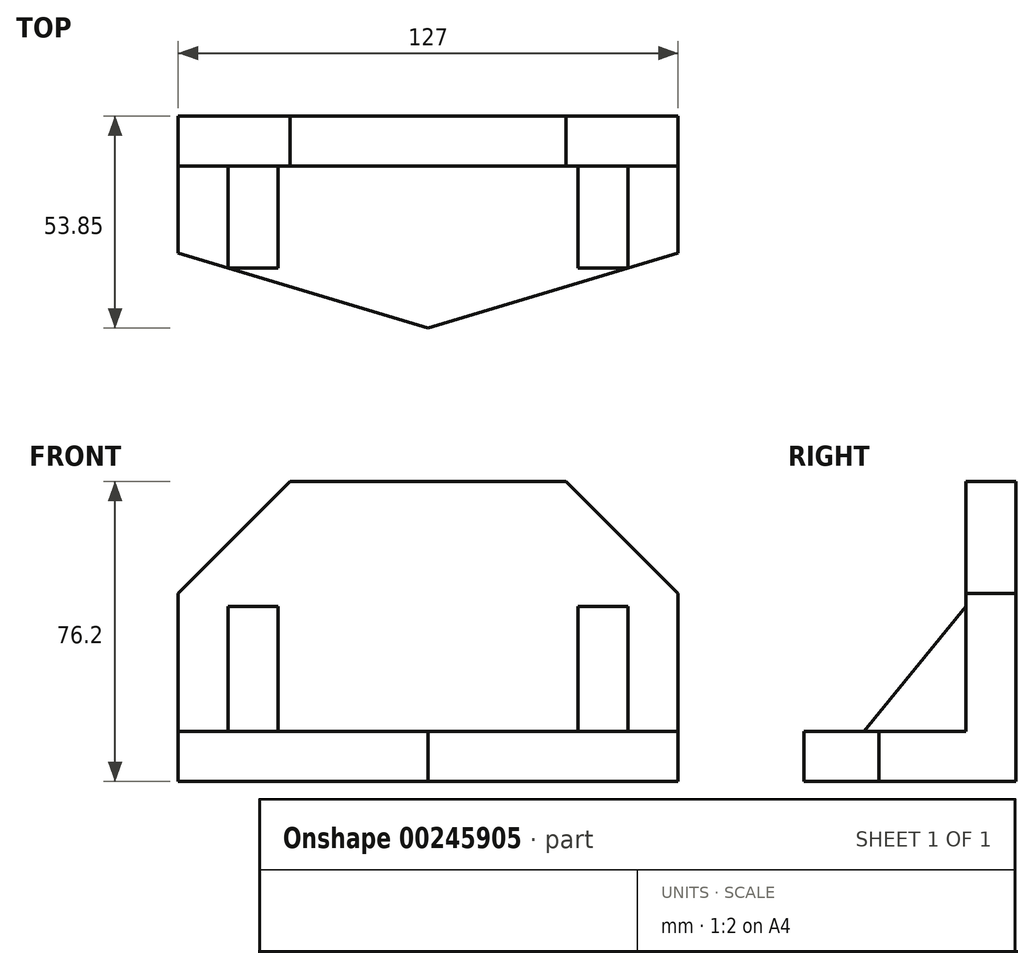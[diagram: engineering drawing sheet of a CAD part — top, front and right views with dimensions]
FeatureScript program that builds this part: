
annotation { "Feature Type Name" : "Feature", "Feature Type Description" : "" }
export const myFeature = defineFeature(function(context is Context, id is Id, definition is map)
    precondition{}
    {
        {
            var Q0;
            Q0=qCreatedBy(makeId("Front.planeOp"),FACE);
            var sketch = newSketch(context, id + "F0", { "sketchPlane" : qUnion([Q0])});
            skLineSegment(sketch, "E0", {"start": v(-81, -38.68) * mm, "end": v(46, -38.68) * mm});
            skLineSegment(sketch, "E1", {"start": v(46, -38.68) * mm, "end": v(46, 37.52) * mm});
            skLineSegment(sketch, "E2", {"start": v(46, 37.52) * mm, "end": v(-81, 37.52) * mm});
            skLineSegment(sketch, "E3", {"start": v(-81, 37.52) * mm, "end": v(-81, -38.68) * mm});
            skSolve(sketch);
        }
        {
            var Q0;
            Q0 = qSketchRegion(id + "F0", true);
            extrude(context, id + "F1", {"entities" : qUnion([Q0]), "depth" : 53.85 * mm});
        }
        {
            var Q0;
            Q0=makeQuery(id+"F1.opExtrude","SWEPT_FACE",FACE,{"disambiguationData":[OSD([sQuery(id+"F0.wireOp",EDGE,"E1")])]});
            var sketch = newSketch(context, id + "F2", { "sketchPlane" : qUnion([Q0])});
            skLineSegment(sketch, "E4", {"start": v(-53.85, 37.52) * mm, "end": v(-12.7, 37.52) * mm});
            skLineSegment(sketch, "E5", {"start": v(-12.7, 37.52) * mm, "end": v(-12.7, -25.98) * mm});
            skLineSegment(sketch, "E6", {"start": v(-12.7, -25.98) * mm, "end": v(-53.85, -25.98) * mm});
            skLineSegment(sketch, "E7", {"start": v(-53.85, -25.98) * mm, "end": v(-53.85, 37.52) * mm});
            skSolve(sketch);
        }
        {
            var Q0;
            Q0 = qSketchRegion(id + "F2", true);
            extrude(context, id + "F3", {"entities" : qUnion([Q0]), "operationType" : NewBodyOperationType.REMOVE, "oppositeDirection" : true, "depth" : 127 * mm});
        }
        {
            var Q0;
            Q0=makeQuery(id+"F3.boolean.opBoolean","COPY",FACE,{"derivedFrom":makeQuery(id+"F3.opExtrude","SWEPT_FACE",FACE,{"disambiguationData":[OSD([sQuery(id+"F2.wireOp",EDGE,"E5")])]})});
            var sketch = newSketch(context, id + "F4", { "sketchPlane" : qUnion([Q0])});
            skLineSegment(sketch, "E8", {"start": v(46, 37.52) * mm, "end": v(17.55, 37.52) * mm});
            skLineSegment(sketch, "E9", {"start": v(46, 37.52) * mm, "end": v(46, 9.07) * mm});
            skLineSegment(sketch, "E10", {"start": v(17.55, 37.52) * mm, "end": v(46, 9.07) * mm});
            skLineSegment(sketch, "E11", {"start": v(-81, 37.52) * mm, "end": v(-52.56, 37.52) * mm});
            skLineSegment(sketch, "E12", {"start": v(-81, 37.52) * mm, "end": v(-81, 9.07) * mm});
            skLineSegment(sketch, "E13", {"start": v(-52.56, 37.52) * mm, "end": v(-81, 9.07) * mm});
            skSolve(sketch);
        }
        {
            var Q0;
            Q0 = qSketchRegion(id + "F4", true);
            extrude(context, id + "F5", {"entities" : qUnion([Q0]), "operationType" : NewBodyOperationType.REMOVE, "oppositeDirection" : true, "depth" : 12.7 * mm});
        }
        {
            var Q0;
            Q0=makeQuery(id+"F3.boolean.opBoolean","COPY",FACE,{"derivedFrom":makeQuery(id+"F3.opExtrude","SWEPT_FACE",FACE,{"disambiguationData":[OSD([sQuery(id+"F2.wireOp",EDGE,"E6")])]})});
            var sketch = newSketch(context, id + "F6", { "sketchPlane" : qUnion([Q0])});
            skLineSegment(sketch, "E14", {"start": v(-17.5, -53.85) * mm, "end": v(46, -53.85) * mm});
            skLineSegment(sketch, "E15", {"start": v(-17.5, -53.85) * mm, "end": v(-81, -53.85) * mm});
            skLineSegment(sketch, "E16", {"start": v(46, -53.85) * mm, "end": v(46, -34.8) * mm});
            skLineSegment(sketch, "E17", {"start": v(-17.5, -53.85) * mm, "end": v(46, -34.8) * mm});
            skLineSegment(sketch, "E18", {"start": v(-81, -53.85) * mm, "end": v(-81, -34.8) * mm});
            skLineSegment(sketch, "E19", {"start": v(-81, -34.8) * mm, "end": v(-17.5, -53.85) * mm});
            skSolve(sketch);
        }
        {
            var Q0;
            Q0 = qSketchRegion(id + "F6", true);
            extrude(context, id + "F7", {"entities" : qUnion([Q0]), "operationType" : NewBodyOperationType.REMOVE, "oppositeDirection" : true, "depth" : 12.7 * mm});
        }
        {
            var Q0;
            Q0=makeQuery(id+"F3.boolean.opBoolean","COPY",FACE,{"derivedFrom":makeQuery(id+"F3.opExtrude","SWEPT_FACE",FACE,{"disambiguationData":[OSD([sQuery(id+"F2.wireOp",EDGE,"E6")])]})});
            var sketch = newSketch(context, id + "F8", { "sketchPlane" : qUnion([Q0])});
            skLineSegment(sketch, "E20", {"start": v(46, -12.7) * mm, "end": v(33.3, -12.7) * mm});
            skLineSegment(sketch, "E21", {"start": v(33.3, -12.7) * mm, "end": v(33.3, -38.6) * mm});
            skLineSegment(sketch, "E22", {"start": v(33.3, -38.6) * mm, "end": v(20.6, -38.6) * mm});
            skLineSegment(sketch, "E23", {"start": v(20.6, -38.6) * mm, "end": v(20.6, -12.7) * mm});
            skLineSegment(sketch, "E24", {"start": v(20.6, -12.7) * mm, "end": v(33.3, -12.7) * mm});
            skLineSegment(sketch, "E25", {"start": v(-81, -12.7) * mm, "end": v(-68.3, -12.7) * mm});
            skLineSegment(sketch, "E26", {"start": v(-68.3, -12.7) * mm, "end": v(-55.6, -12.7) * mm});
            skLineSegment(sketch, "E27", {"start": v(-68.3, -12.7) * mm, "end": v(-68.3, -38.6) * mm});
            skLineSegment(sketch, "E28", {"start": v(-68.3, -38.6) * mm, "end": v(-55.6, -38.6) * mm});
            skLineSegment(sketch, "E29", {"start": v(-55.6, -38.6) * mm, "end": v(-55.6, -12.7) * mm});
            skSolve(sketch);
        }
        {
            var Q0;
            Q0 = qSketchRegion(id + "F8", true);
            extrude(context, id + "F9", {"entities" : qUnion([Q0]), "operationType" : NewBodyOperationType.ADD, "depth" : 31.75 * mm});
        }
        {
            var Q0;
            Q0=makeQuery(id+"F9.opExtrude","SWEPT_FACE",FACE,{"disambiguationData":[OSD([sQuery(id+"F8.wireOp",EDGE,"E21")])]});
            var sketch = newSketch(context, id + "F10", { "sketchPlane" : qUnion([Q0])});
            skLineSegment(sketch, "E30", {"start": v(-12.7, 5.77) * mm, "end": v(-38.6, -25.98) * mm});
            skLineSegment(sketch, "E31", {"start": v(-38.6, -25.98) * mm, "end": v(-38.6, 5.77) * mm});
            skLineSegment(sketch, "E32", {"start": v(-38.6, 5.77) * mm, "end": v(-12.7, 5.77) * mm});
            skSolve(sketch);
        }
        {
            var Q0;
            Q0 = qSketchRegion(id + "F10", true);
            extrude(context, id + "F11", {"entities" : qUnion([Q0]), "operationType" : NewBodyOperationType.REMOVE, "oppositeDirection" : true, "depth" : 12.7 * mm});
        }
        {
            var Q0;
            Q0=makeQuery(id+"F9.opExtrude","SWEPT_FACE",FACE,{"disambiguationData":[OSD([sQuery(id+"F8.wireOp",EDGE,"E29")])]});
            var sketch = newSketch(context, id + "F12", { "sketchPlane" : qUnion([Q0])});
            skLineSegment(sketch, "E33", {"start": v(-12.7, 5.77) * mm, "end": v(-38.6, -25.98) * mm});
            skLineSegment(sketch, "E34", {"start": v(-38.6, -25.98) * mm, "end": v(-38.6, 5.77) * mm});
            skLineSegment(sketch, "E35", {"start": v(-38.6, 5.77) * mm, "end": v(-12.7, 5.77) * mm});
            skSolve(sketch);
        }
        {
            var Q0;
            Q0 = qSketchRegion(id + "F12", true);
            extrude(context, id + "F13", {"entities" : qUnion([Q0]), "operationType" : NewBodyOperationType.REMOVE, "oppositeDirection" : true, "depth" : 12.7 * mm});
        }
    });
